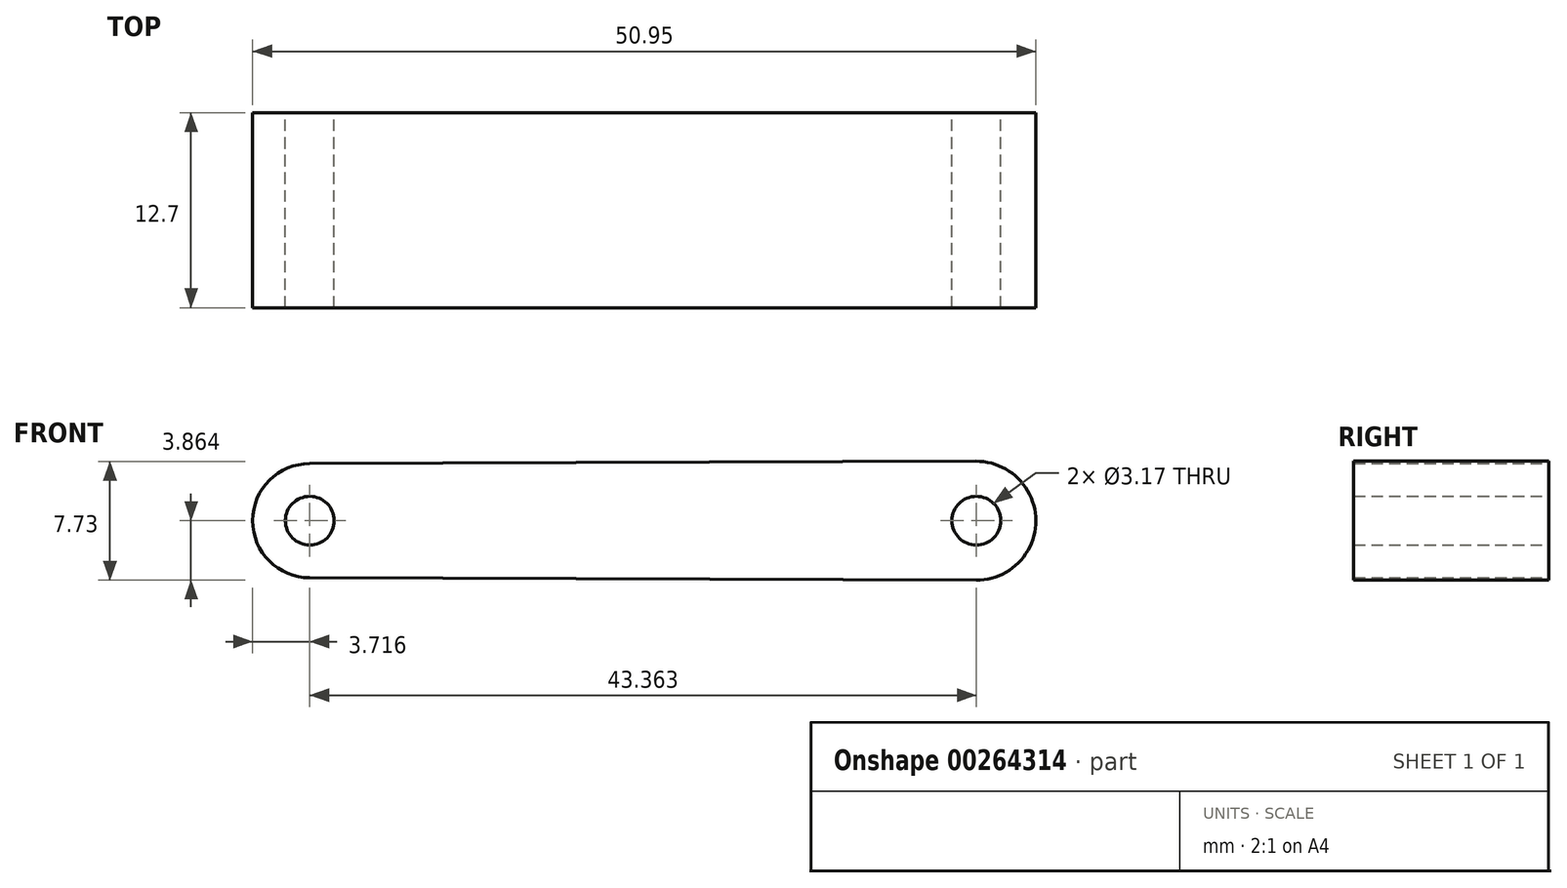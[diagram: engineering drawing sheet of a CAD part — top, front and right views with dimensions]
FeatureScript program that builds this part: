
annotation { "Feature Type Name" : "Feature", "Feature Type Description" : "" }
export const myFeature = defineFeature(function(context is Context, id is Id, definition is map)
    precondition{}
    {
        {
            var Q0;
            Q0=qCreatedBy(makeId("Front.planeOp"),FACE);
            var sketch = newSketch(context, id + "F0", { "sketchPlane" : qUnion([Q0])});
            skArc(sketch, "E0", {"start": v(-55.57, 28.46) * mm, "mid": v(-59.3, 24.74) * mm, "end": v(-55.57, 21.03) * mm});
            skCircle(sketch, "E1", {"center": v(-55.57, 24.74) * mm, "radius": 1.59 * mm});
            skCircle(sketch, "E2", {"center": v(-12.21, 24.74) * mm, "radius": 1.59 * mm});
            skArc(sketch, "E3", {"start": v(-12.22, 20.88) * mm, "mid": v(-8.34, 24.75) * mm, "end": v(-12.24, 28.61) * mm});
            skLineSegment(sketch, "E4", {"start": v(-55.57, 28.46) * mm, "end": v(-12.21, 28.61) * mm});
            skLineSegment(sketch, "E5", {"start": v(-55.57, 21.03) * mm, "end": v(-12.22, 20.88) * mm});
            skSolve(sketch);
        }
        {
            var Q0;
            Q0 = qSketchRegion(id + "F0", true);
            extrude(context, id + "F1", {"entities" : qUnion([Q0]), "depth" : 12.7 * mm});
        }
    });
